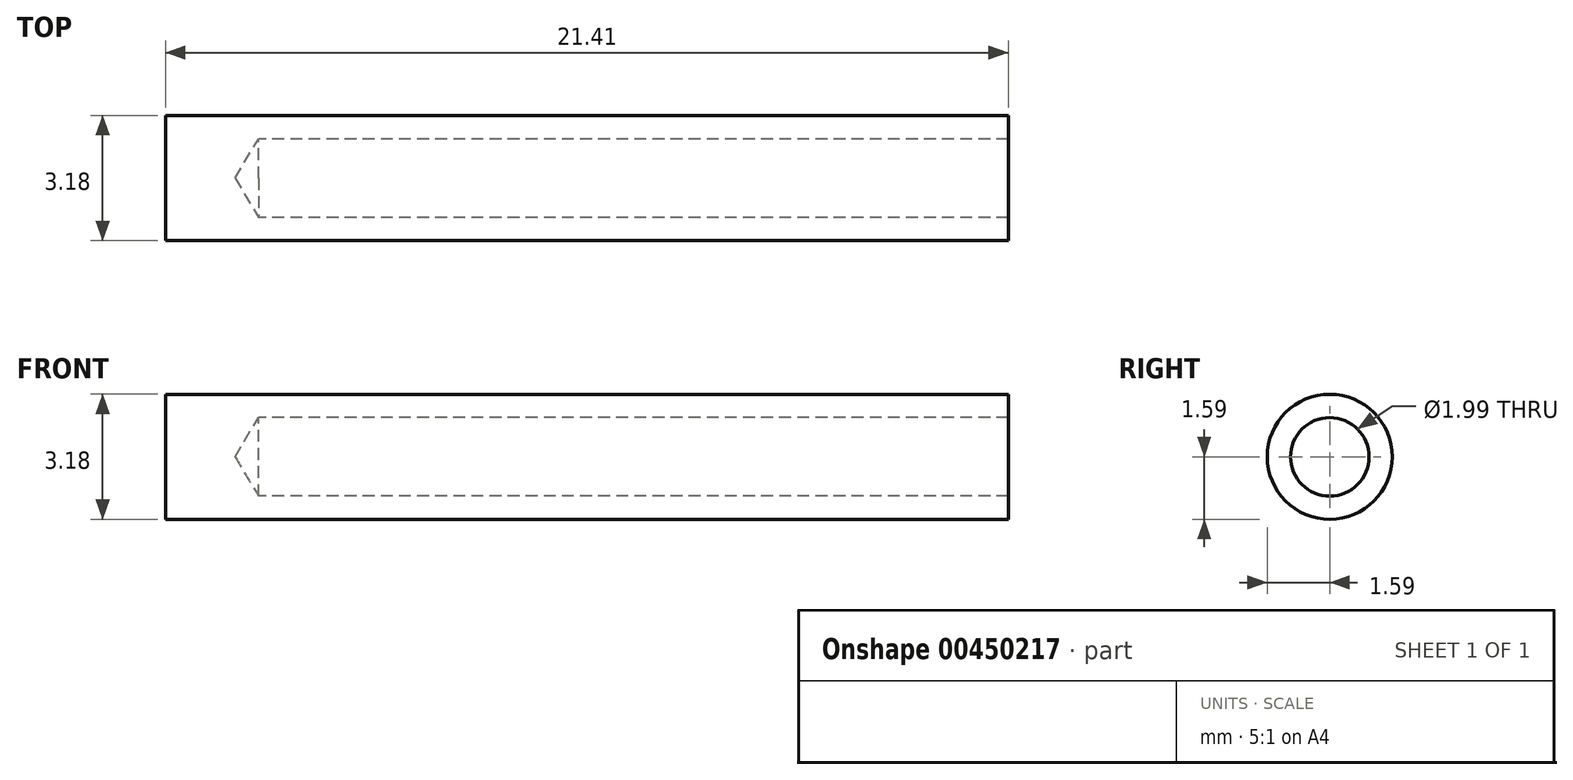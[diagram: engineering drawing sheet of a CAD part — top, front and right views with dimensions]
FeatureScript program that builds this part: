
annotation { "Feature Type Name" : "Feature", "Feature Type Description" : "" }
export const myFeature = defineFeature(function(context is Context, id is Id, definition is map)
    precondition{}
    {
        {
            var Q0;
            Q0=qCreatedBy(makeId("Right.planeOp"),FACE);
            var sketch = newSketch(context, id + "F0", { "sketchPlane" : qUnion([Q0])});
            skCircle(sketch, "E0", {"center": v(0, 0) * mm, "radius": 1.59 * mm});
            skSolve(sketch);
        }
        {
            var Q0;
            Q0 = qSketchRegion(id + "F0", true);
            extrude(context, id + "F1", {"entities" : qUnion([Q0]), "oppositeDirection" : true, "depth" : 21.41 * mm});
        }
        {
            var Q0;
            Q0=makeQuery(id+"F1.opExtrude","CAP_FACE",FACE,{"disambiguationData":[OSD([sQuery(id+"F0.wireOp",EDGE,"E0")])],"isStart":true});
            var sketch = newSketch(context, id + "F2", { "sketchPlane" : qUnion([Q0])});
            skPoint(sketch, "E1", {"position": v(0, 0) * mm});
            skSolve(sketch);
        }
        {
            var Q0;
            Q0=sQuery(id+"F2.wireOp",VERTEX,"E1");
            var Q1;
            Q1=makeQuery(id+"F1.opExtrude","SWEPT_BODY",BODY,{"disambiguationData":[OSD([sQuery(id+"F0.wireOp",EDGE,"E0")])]});
            hole(context, id + "F3", {"style" : HoleStyle.SIMPLE, "endStyle" : HoleEndStyle.BLIND, "holeDiameter" : 2 * mm, "holeDepth" : 19.05 * mm, "isTappedThrough" : true, "tappedDepth" : 5.7 * mm, "tapClearance" : 3, "locations" : qUnion([Q0]), "scope" : qUnion([Q1]), "startStyle" : HoleStartStyle.SKETCH});
        }
    });
